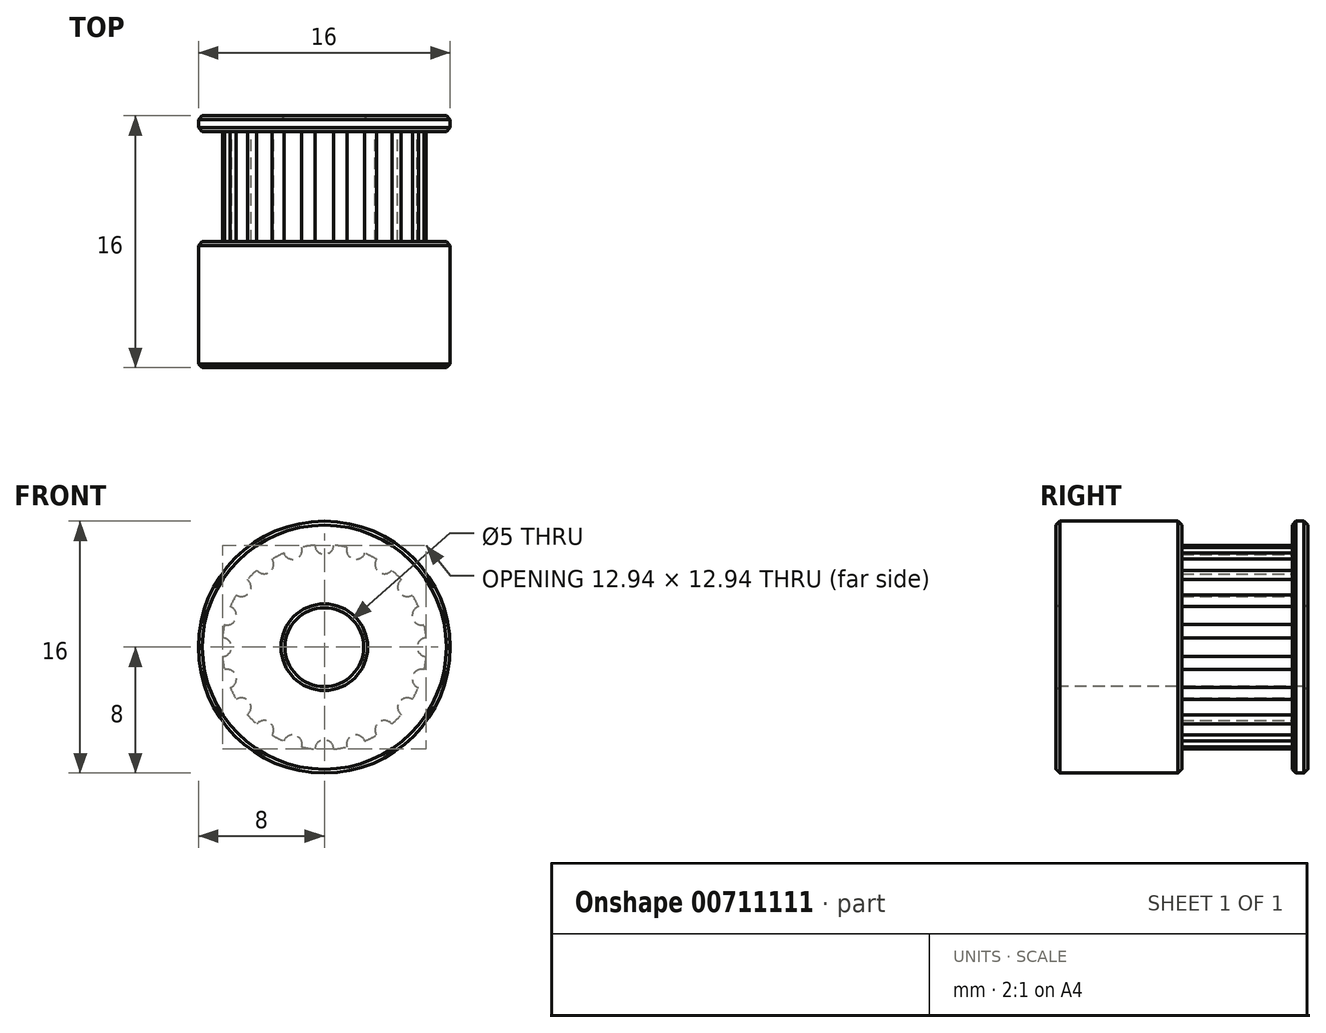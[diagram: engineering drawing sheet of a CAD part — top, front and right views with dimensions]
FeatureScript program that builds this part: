
annotation { "Feature Type Name" : "Feature", "Feature Type Description" : "" }
export const myFeature = defineFeature(function(context is Context, id is Id, definition is map)
    precondition{}
    {
        {
            var Q0;
            Q0=qCreatedBy(makeId("Front.planeOp"),FACE);
            var sketch = newSketch(context, id + "F0", { "sketchPlane" : qUnion([Q0])});
            skCircle(sketch, "E0", {"center": v(0, 0) * mm, "radius": 8 * mm});
            skSolve(sketch);
        }
        {
            var Q0;
            Q0=makeQuery(id+"F0.imprint","IMPRINT",FACE,{"disambiguationData":[TD([[makeQuery(id+"F0.imprint","IMPRINT",EDGE,{"derivedFrom":sQuery(id+"F0.wireOp",EDGE,"E0")}),1.0]])]});
            extrude(context, id + "F1", {"entities" : qUnion([Q0]), "depth" : 1 * mm, "offsetDistance" : 25 * mm});
        }
        {
            var Q0;
            Q0=makeQuery(id+"F1.opExtrude","CAP_FACE",FACE,{"disambiguationData":[OSD([sQuery(id+"F0.wireOp",EDGE,"E0")])],"isStart":false});
            var sketch = newSketch(context, id + "F2", { "sketchPlane" : qUnion([Q0])});
            skCircle(sketch, "E1", {"center": v(0, 0) * mm, "radius": 6.5 * mm});
            skSolve(sketch);
        }
        {
            var Q0;
            Q0=qSketchRegion(id+"F2",true);
            extrude(context, id + "F3", {"entities" : qUnion([Q0]), "operationType" : NewBodyOperationType.ADD, "depth" : 7 * mm, "offsetDistance" : 25 * mm});
        }
        {
            var Q0;
            Q0=makeQuery(id+"F3.opExtrude","CAP_FACE",FACE,{"disambiguationData":[OSD([sQuery(id+"F2.wireOp",EDGE,"E1")])],"isStart":false});
            var sketch = newSketch(context, id + "F4", { "sketchPlane" : qUnion([Q0])});
            skCircle(sketch, "E2", {"center": v(0, 0) * mm, "radius": 8 * mm});
            skSolve(sketch);
        }
        {
            var Q0;
            Q0=qSketchRegion(id+"F4",true);
            extrude(context, id + "F5", {"entities" : qUnion([Q0]), "operationType" : NewBodyOperationType.ADD, "depth" : 8 * mm, "offsetDistance" : 25 * mm});
        }
        {
            var Q0;
            Q0=makeQuery(id+"F1.opExtrude","CAP_FACE",FACE,{"disambiguationData":[OSD([sQuery(id+"F0.wireOp",EDGE,"E0")])],"isStart":false});
            var sketch = newSketch(context, id + "F6", { "sketchPlane" : qUnion([Q0])});
            skCircle(sketch, "E3", {"center": v(0, 0) * mm, "radius": 5 * mm, "construction": true});
            skLineSegment(sketch, "E4", {"start": v(-6.5, 0) * mm, "end": v(0, 0) * mm, "construction": true});
            skLineSegment(sketch, "E5", {"start": v(0, 0) * mm, "end": v(0, 6.5) * mm, "construction": true});
            skCircle(sketch, "E6", {"center": v(0, 6.5) * mm, "radius": 0.6 * mm});
            skCircle(sketch, "E7.1.0", {"center": v(-2, 6.18) * mm, "radius": 0.6 * mm});
            skCircle(sketch, "E7.2.0", {"center": v(-3.82, 5.26) * mm, "radius": 0.6 * mm});
            skCircle(sketch, "E7.3.0", {"center": v(-5.26, 3.82) * mm, "radius": 0.6 * mm});
            skCircle(sketch, "E7.4.0", {"center": v(-6.18, 2) * mm, "radius": 0.6 * mm});
            skCircle(sketch, "E7.5.0", {"center": v(-6.5, 0) * mm, "radius": 0.6 * mm});
            skCircle(sketch, "E7.6.0", {"center": v(-6.18, -2) * mm, "radius": 0.6 * mm});
            skCircle(sketch, "E7.7.0", {"center": v(-5.26, -3.82) * mm, "radius": 0.6 * mm});
            skCircle(sketch, "E7.8.0", {"center": v(-3.82, -5.26) * mm, "radius": 0.6 * mm});
            skCircle(sketch, "E7.9.0", {"center": v(-2, -6.18) * mm, "radius": 0.6 * mm});
            skCircle(sketch, "E7.10.0", {"center": v(0, -6.5) * mm, "radius": 0.6 * mm});
            skCircle(sketch, "E7.11.0", {"center": v(2, -6.18) * mm, "radius": 0.6 * mm});
            skCircle(sketch, "E7.12.0", {"center": v(3.82, -5.26) * mm, "radius": 0.6 * mm});
            skCircle(sketch, "E7.13.0", {"center": v(5.26, -3.82) * mm, "radius": 0.6 * mm});
            skCircle(sketch, "E7.14.0", {"center": v(6.18, -2) * mm, "radius": 0.6 * mm});
            skCircle(sketch, "E7.15.0", {"center": v(6.5, 0) * mm, "radius": 0.6 * mm});
            skCircle(sketch, "E8.1.16.0", {"center": v(6.18, 2) * mm, "radius": 0.6 * mm});
            skCircle(sketch, "E8.1.17.0", {"center": v(5.26, 3.82) * mm, "radius": 0.6 * mm});
            skCircle(sketch, "E8.1.18.0", {"center": v(3.82, 5.26) * mm, "radius": 0.6 * mm});
            skCircle(sketch, "E8.1.19.0", {"center": v(2, 6.18) * mm, "radius": 0.6 * mm});
            skSolve(sketch);
        }
        {
            var Q0;
            Q0=qSketchRegion(id+"F6",true);
            var Q1;
            Q1=makeQuery(id+"F5.opExtrude","CAP_FACE",FACE,{"disambiguationData":[OSD([sQuery(id+"F4.wireOp",EDGE,"E2")])],"isStart":true});
            extrude(context, id + "F7", {"entities" : qUnion([Q0]), "operationType" : NewBodyOperationType.REMOVE, "endBound" : BoundingType.UP_TO_SURFACE, "depth" : 7.5 * mm, "endBoundEntityFace" : qUnion([Q1]), "offsetDistance" : 25 * mm});
        }
        {
            var Q0;
            Q0=makeQuery(id+"F5.opExtrude","CAP_FACE",FACE,{"disambiguationData":[OSD([sQuery(id+"F4.wireOp",EDGE,"E2")])],"isStart":false});
            var sketch = newSketch(context, id + "F8", { "sketchPlane" : qUnion([Q0])});
            skCircle(sketch, "E9", {"center": v(0, 0) * mm, "radius": 2.5 * mm});
            skSolve(sketch);
        }
        {
            var Q0;
            Q0=qSketchRegion(id+"F8",true);
            extrude(context, id + "F9", {"entities" : qUnion([Q0]), "operationType" : NewBodyOperationType.REMOVE, "endBound" : BoundingType.THROUGH_ALL, "oppositeDirection" : true, "depth" : 25 * mm, "offsetDistance" : 25 * mm});
        }
        {
            var Q0;
            Q0=makeQuery(id+"F5.opExtrude","SWEPT_FACE",FACE,{"disambiguationData":[OSD([sQuery(id+"F4.wireOp",EDGE,"E2")])]});
            var Q1;
            Q1=makeQuery(id+"F1.opExtrude","SWEPT_FACE",FACE,{"disambiguationData":[OSD([sQuery(id+"F0.wireOp",EDGE,"E0")])]});
            var Q2;
            Q2=makeQuery(id+"F9.boolean.opBoolean","COPY",FACE,{"derivedFrom":makeQuery(id+"F9.opExtrude","SWEPT_FACE",FACE,{"disambiguationData":[OSD([sQuery(id+"F8.wireOp",EDGE,"E9")])]})});
            chamfer(context, id + "F10", {"entities" : qUnion([Q0, Q1, Q2]), "width" : 0.25 * mm, "tangentPropagation" : true});
        }
    });
